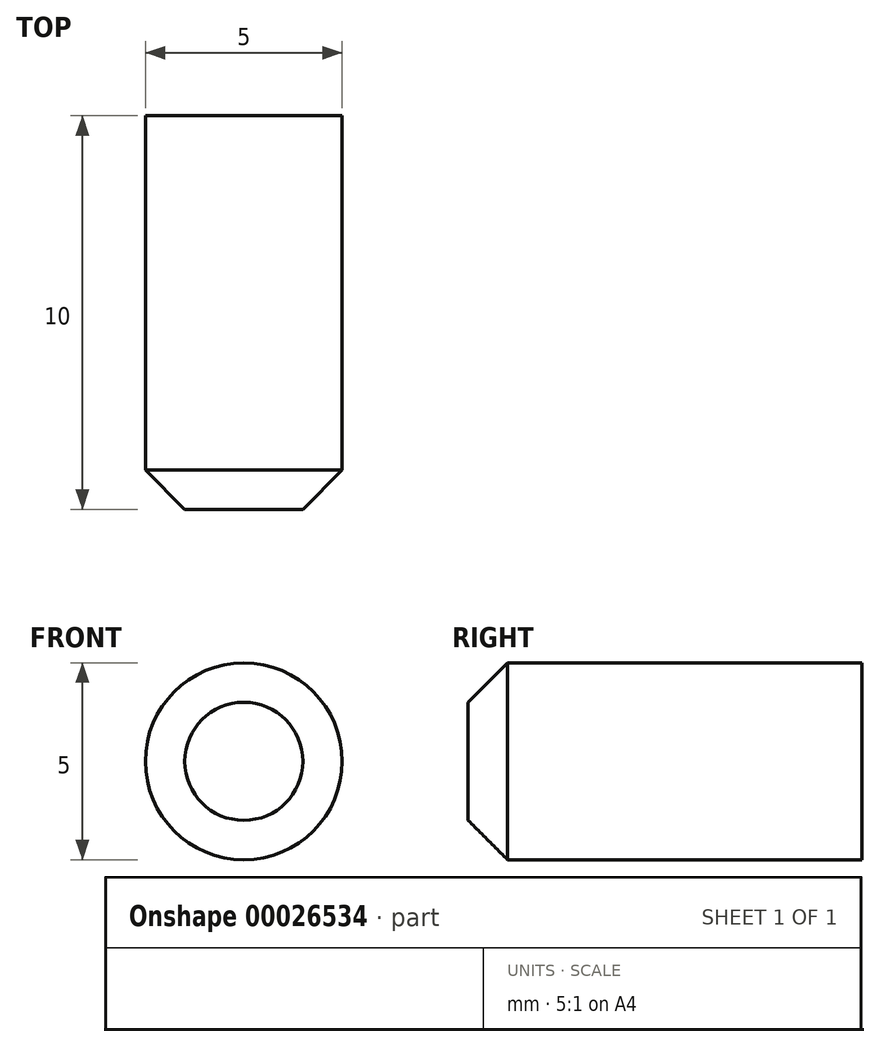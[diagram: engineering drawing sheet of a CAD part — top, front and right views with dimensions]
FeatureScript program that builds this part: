
annotation { "Feature Type Name" : "Feature", "Feature Type Description" : "" }
export const myFeature = defineFeature(function(context is Context, id is Id, definition is map)
    precondition{}
    {
        {
            var Q0;
            Q0=qCreatedBy(makeId("Front.planeOp"),FACE);
            var sketch = newSketch(context, id + "F0", { "sketchPlane" : qUnion([Q0])});
            skCircle(sketch, "E0", {"center": v(0, 0) * mm, "radius": 2.5 * mm});
            skSolve(sketch);
        }
        {
            var Q0;
            Q0 = qSketchRegion(id + "F0", true);
            extrude(context, id + "F1", {"entities" : qUnion([Q0]), "depth" : 10 * mm});
        }
        {
            var Q0;
            Q0=makeQuery(id+"F1.opExtrude","CAP_EDGE",EDGE,{"disambiguationData":[OSD([sQuery(id+"F0.wireOp",EDGE,"E0")])],"isStart":false});
            chamfer(context, id + "F2", {"entities" : qUnion([Q0]), "width" : 1 * mm, "tangentPropagation" : true});
        }
    });
